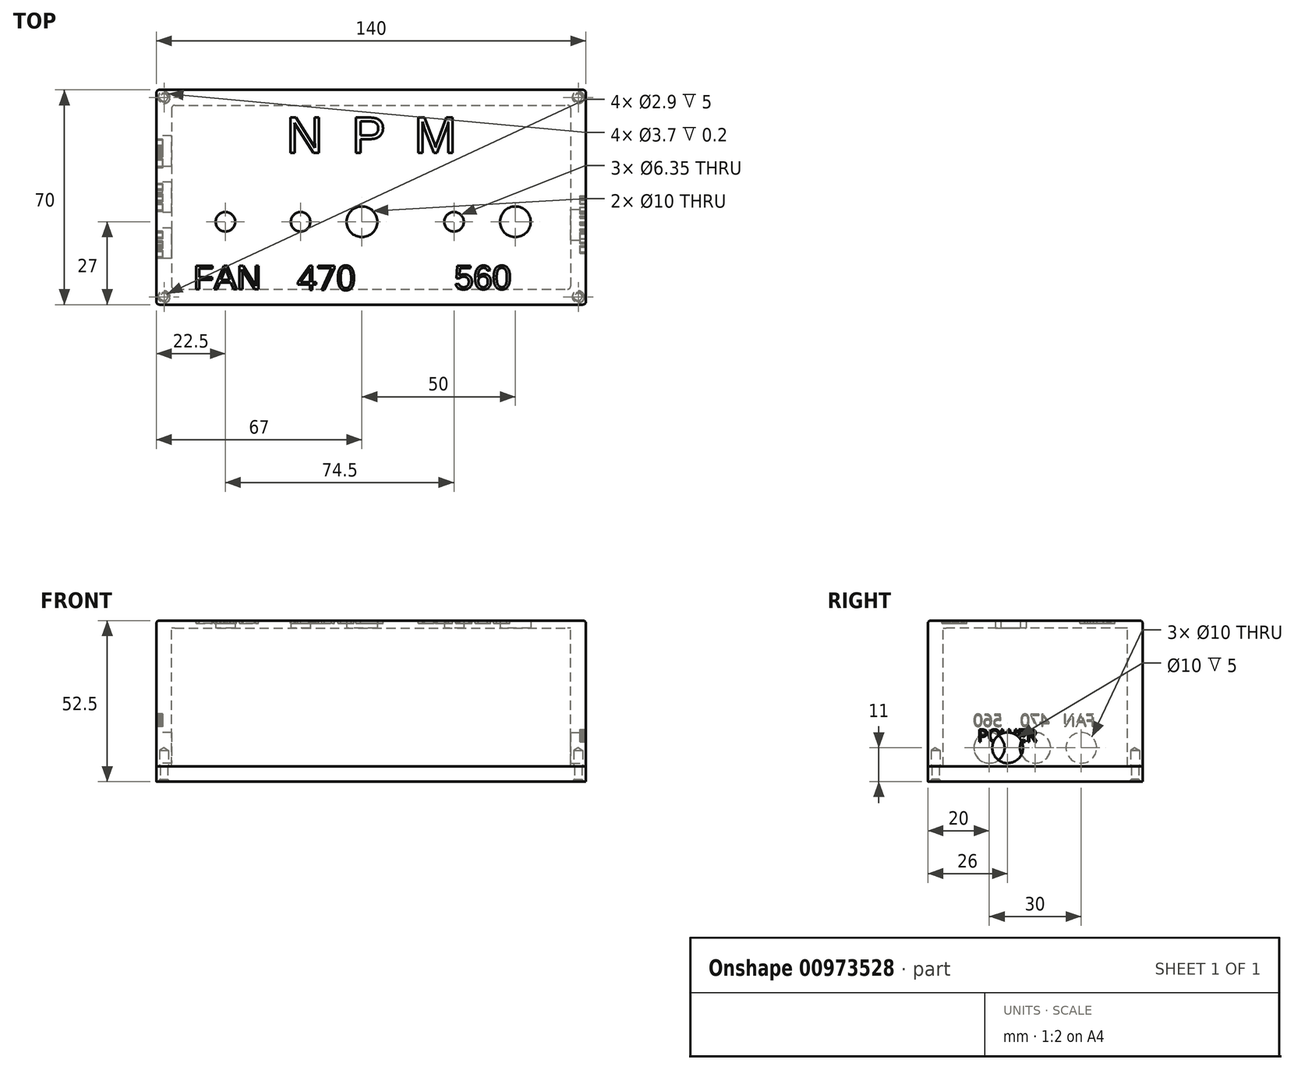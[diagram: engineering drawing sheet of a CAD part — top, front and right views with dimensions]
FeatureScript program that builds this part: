
annotation { "Feature Type Name" : "Feature", "Feature Type Description" : "" }
export const myFeature = defineFeature(function(context is Context, id is Id, definition is map)
    precondition{}
    {
        {
            var Q0;
            Q0=qCreatedBy(makeId("Top.planeOp"),FACE);
            var sketch = newSketch(context, id + "F0", { "sketchPlane" : qUnion([Q0])});
            skLineSegment(sketch, "E0.bottom", {"start": v(0, 0) * mm, "end": v(140, 0) * mm});
            skLineSegment(sketch, "E0.top", {"start": v(0, 70) * mm, "end": v(140, 70) * mm});
            skLineSegment(sketch, "E0.left", {"start": v(0, 0) * mm, "end": v(0, 70) * mm});
            skLineSegment(sketch, "E0.right", {"start": v(140, 0) * mm, "end": v(140, 70) * mm});
            skCircle(sketch, "E1", {"center": v(117, 27) * mm, "radius": 5 * mm});
            skCircle(sketch, "E2", {"center": v(67, 27) * mm, "radius": 5 * mm});
            skCircle(sketch, "E3", {"center": v(22.5, 27) * mm, "radius": 3.18 * mm});
            skLineSegment(sketch, "E4", {"start": v(5, 70) * mm, "end": v(5, 5) * mm, "construction": true});
            skLineSegment(sketch, "E5", {"start": v(5, 5) * mm, "end": v(135, 5) * mm, "construction": true});
            skLineSegment(sketch, "E6", {"start": v(135, 5) * mm, "end": v(135, 70) * mm, "construction": true});
            skLineSegment(sketch, "E7", {"start": v(0, 65) * mm, "end": v(140, 65) * mm, "construction": true});
            skLineSegment(sketch, "E8", {"start": v(5, 5) * mm, "end": v(0, 5) * mm, "construction": true});
            skLineSegment(sketch, "E9", {"start": v(135, 5) * mm, "end": v(140, 5) * mm, "construction": true});
            skPoint(sketch, "E10.endSnap0", {"position": v(5, 37.5) * mm});
            skLineSegment(sketch, "E11", {"start": v(5, 70) * mm, "end": v(135, 65) * mm, "construction": true});
            skLineSegment(sketch, "E12", {"start": v(135, 70) * mm, "end": v(5, 65) * mm, "construction": true});
            skLineSegment(sketch, "E13", {"start": v(140, 5) * mm, "end": v(0, 0) * mm, "construction": true});
            skLineSegment(sketch, "E14", {"start": v(0, 5) * mm, "end": v(140, 0) * mm, "construction": true});
            skPoint(sketch, "E15", {"position": v(70, 2.5) * mm});
            skPoint(sketch, "E16", {"position": v(70, 67.5) * mm});
            skLineSegment(sketch, "E17", {"start": v(5, 27) * mm, "end": v(135, 27) * mm, "construction": true});
            skCircle(sketch, "E18", {"center": v(47, 27) * mm, "radius": 3.18 * mm});
            skCircle(sketch, "E19", {"center": v(97, 27) * mm, "radius": 3.18 * mm});
            skSolve(sketch);
        }
        {
            var Q0;
            Q0=makeQuery(id+"F0.imprint","IMPRINT",FACE,{"disambiguationData":[TD([[makeQuery(id+"F0.imprint","IMPRINT",EDGE,{"derivedFrom":sQuery(id+"F0.wireOp",EDGE,"E0.bottom")}),1.0]])]});
            extrude(context, id + "F1", {"entities" : qUnion([Q0]), "depth" : 2.5 * mm, "offsetDistance" : 25 * mm});
        }
        {
            var Q0;
            Q0=makeQuery(id+"F1.opExtrude","CAP_FACE",FACE,{"disambiguationData":[OSD([sQuery(id+"F0.wireOp",EDGE,"E0.bottom"),sQuery(id+"F0.wireOp",EDGE,"E0.top"),sQuery(id+"F0.wireOp",EDGE,"E0.left"),sQuery(id+"F0.wireOp",EDGE,"E0.right"),sQuery(id+"F0.wireOp",EDGE,"E1"),sQuery(id+"F0.wireOp",EDGE,"E2"),sQuery(id+"F0.wireOp",EDGE,"E3")])],"isStart":true});
            var sketch = newSketch(context, id + "F2", { "sketchPlane" : qUnion([Q0])});
            skLineSegment(sketch, "E20.bottom", {"start": v(0, -70) * mm, "end": v(140, -70) * mm, "construction": true});
            skLineSegment(sketch, "E20.top", {"start": v(0, 0) * mm, "end": v(140, 0) * mm, "construction": true});
            skLineSegment(sketch, "E20.left", {"start": v(0, -70) * mm, "end": v(0, 0) * mm, "construction": true});
            skLineSegment(sketch, "E20.right", {"start": v(140, -70) * mm, "end": v(140, 0) * mm, "construction": true});
            skLineSegment(sketch, "E21.bottom", {"start": v(5, -65) * mm, "end": v(135, -65) * mm});
            skLineSegment(sketch, "E21.top", {"start": v(5, -5) * mm, "end": v(135, -5) * mm});
            skLineSegment(sketch, "E21.left", {"start": v(5, -65) * mm, "end": v(5, -5) * mm});
            skLineSegment(sketch, "E21.right", {"start": v(135, -65) * mm, "end": v(135, -5) * mm});
            skSolve(sketch);
        }
        {
            var Q0;
            Q0=makeQuery(id+"F2.imprint","IMPRINT",FACE,{"disambiguationData":[TD([[makeQuery(id+"F2.imprint","IMPRINT",EDGE,{"derivedFrom":sQuery(id+"F2.wireOp",EDGE,"E21.bottom")}),-1.0]])]});
            var Q1;
            Q1=makeQuery(id+"F2.imprint","IMPRINT",FACE,{"disambiguationData":[TD([[makeQuery(id+"F2.imprint","IMPRINT",EDGE,{"derivedFrom":makeQuery(id+"FxvTJw6m9mzOm3c_1.hole-0.boolean.opBoolean","INTERSECT",EDGE,{"derivedFrom":[makeQuery(id+"F1.opExtrude","CAP_FACE",FACE,{"disambiguationData":[OSD([sQuery(id+"F0.wireOp",EDGE,"E0.bottom"),sQuery(id+"F0.wireOp",EDGE,"E0.top"),sQuery(id+"F0.wireOp",EDGE,"E0.left"),sQuery(id+"F0.wireOp",EDGE,"E0.right"),sQuery(id+"F0.wireOp",EDGE,"E1"),sQuery(id+"F0.wireOp",EDGE,"E2"),sQuery(id+"F0.wireOp",EDGE,"E3")])],"isStart":true}),makeQuery(id+"FxvTJw6m9mzOm3c_1.hole-0.opRevolve","SWEPT_FACE",FACE,{"disambiguationData":[OSD([sQuery(id+"FxvTJw6m9mzOm3c_1.hole-0.sketch.wireOp",EDGE,"core_line_2")])]})]})}),1.0]])]});
            var Q2;
            Q2=makeQuery(id+"F2.imprint","IMPRINT",FACE,{"disambiguationData":[TD([[makeQuery(id+"F2.imprint","IMPRINT",EDGE,{"derivedFrom":makeQuery(id+"FxvTJw6m9mzOm3c_1.hole-1.boolean.opBoolean","INTERSECT",EDGE,{"derivedFrom":[makeQuery(id+"F1.opExtrude","CAP_FACE",FACE,{"disambiguationData":[OSD([sQuery(id+"F0.wireOp",EDGE,"E0.bottom"),sQuery(id+"F0.wireOp",EDGE,"E0.top"),sQuery(id+"F0.wireOp",EDGE,"E0.left"),sQuery(id+"F0.wireOp",EDGE,"E0.right"),sQuery(id+"F0.wireOp",EDGE,"E1"),sQuery(id+"F0.wireOp",EDGE,"E2"),sQuery(id+"F0.wireOp",EDGE,"E3")])],"isStart":true}),makeQuery(id+"FxvTJw6m9mzOm3c_1.hole-1.opRevolve","SWEPT_FACE",FACE,{"disambiguationData":[OSD([sQuery(id+"FxvTJw6m9mzOm3c_1.hole-1.sketch.wireOp",EDGE,"core_line_2")])]})]})}),1.0]])]});
            var Q3;
            Q3=makeQuery(id+"F2.imprint","IMPRINT",FACE,{"disambiguationData":[TD([[makeQuery(id+"F2.imprint","IMPRINT",EDGE,{"derivedFrom":makeQuery(id+"FxvTJw6m9mzOm3c_1.hole-2.boolean.opBoolean","INTERSECT",EDGE,{"derivedFrom":[makeQuery(id+"F1.opExtrude","CAP_FACE",FACE,{"disambiguationData":[OSD([sQuery(id+"F0.wireOp",EDGE,"E0.bottom"),sQuery(id+"F0.wireOp",EDGE,"E0.top"),sQuery(id+"F0.wireOp",EDGE,"E0.left"),sQuery(id+"F0.wireOp",EDGE,"E0.right"),sQuery(id+"F0.wireOp",EDGE,"E1"),sQuery(id+"F0.wireOp",EDGE,"E2"),sQuery(id+"F0.wireOp",EDGE,"E3")])],"isStart":true}),makeQuery(id+"FxvTJw6m9mzOm3c_1.hole-2.opRevolve","SWEPT_FACE",FACE,{"disambiguationData":[OSD([sQuery(id+"FxvTJw6m9mzOm3c_1.hole-2.sketch.wireOp",EDGE,"core_line_2")])]})]})}),1.0]])]});
            var Q4;
            Q4=makeQuery(id+"F2.imprint","IMPRINT",FACE,{"disambiguationData":[TD([[makeQuery(id+"F2.imprint","IMPRINT",EDGE,{"derivedFrom":makeQuery(id+"FxvTJw6m9mzOm3c_1.hole-3.boolean.opBoolean","INTERSECT",EDGE,{"derivedFrom":[makeQuery(id+"F1.opExtrude","CAP_FACE",FACE,{"disambiguationData":[OSD([sQuery(id+"F0.wireOp",EDGE,"E0.bottom"),sQuery(id+"F0.wireOp",EDGE,"E0.top"),sQuery(id+"F0.wireOp",EDGE,"E0.left"),sQuery(id+"F0.wireOp",EDGE,"E0.right"),sQuery(id+"F0.wireOp",EDGE,"E1"),sQuery(id+"F0.wireOp",EDGE,"E2"),sQuery(id+"F0.wireOp",EDGE,"E3")])],"isStart":true}),makeQuery(id+"FxvTJw6m9mzOm3c_1.hole-3.opRevolve","SWEPT_FACE",FACE,{"disambiguationData":[OSD([sQuery(id+"FxvTJw6m9mzOm3c_1.hole-3.sketch.wireOp",EDGE,"core_line_2")])]})]})}),1.0]])]});
            extrude(context, id + "F3", {"entities" : qUnion([Q0, Q1, Q2, Q3, Q4]), "depth" : 45 * mm, "offsetDistance" : 25 * mm});
        }
        {
            var Q0;
            Q0=makeQuery(id+"F3.opExtrude","CAP_FACE",FACE,{"disambiguationData":[OSD([sQuery(id+"F0.wireOp",EDGE,"E0.bottom"),sQuery(id+"F0.wireOp",EDGE,"E0.top"),sQuery(id+"F0.wireOp",EDGE,"E0.left"),sQuery(id+"F0.wireOp",EDGE,"E0.right"),sQuery(id+"F2.wireOp",EDGE,"E21.bottom"),sQuery(id+"F2.wireOp",EDGE,"E21.top"),sQuery(id+"F2.wireOp",EDGE,"E21.left"),sQuery(id+"F2.wireOp",EDGE,"E21.right")])],"isStart":false});
            var sketch = newSketch(context, id + "F4", { "sketchPlane" : qUnion([Q0])});
            skLineSegment(sketch, "E22.bottom", {"start": v(0, 0) * mm, "end": v(140, 0) * mm});
            skLineSegment(sketch, "E22.top", {"start": v(0, -70) * mm, "end": v(140, -70) * mm});
            skLineSegment(sketch, "E22.left", {"start": v(0, 0) * mm, "end": v(0, -70) * mm});
            skLineSegment(sketch, "E22.right", {"start": v(140, 0) * mm, "end": v(140, -70) * mm});
            skLineSegment(sketch, "E23.bottom", {"start": v(5, -5) * mm, "end": v(135, -5) * mm, "construction": true});
            skLineSegment(sketch, "E23.top", {"start": v(5, -65) * mm, "end": v(135, -65) * mm, "construction": true});
            skLineSegment(sketch, "E23.left", {"start": v(5, -5) * mm, "end": v(5, -65) * mm, "construction": true});
            skLineSegment(sketch, "E23.right", {"start": v(135, -5) * mm, "end": v(135, -65) * mm, "construction": true});
            skSolve(sketch);
        }
        {
            var Q0;
            Q0=makeQuery(id+"F4.imprint","IMPRINT",FACE,{"disambiguationData":[TD([[makeQuery(id+"F4.imprint","IMPRINT",EDGE,{"derivedFrom":sQuery(id+"F4.wireOp",EDGE,"E22.bottom")}),-1.0]])]});
            var Q1;
            Q1=makeQuery(id+"F4.imprint","IMPRINT",FACE,{"disambiguationData":[TD([[makeQuery(id+"F4.imprint","IMPRINT",EDGE,{"derivedFrom":makeQuery(id+"F3.opExtrude","CAP_EDGE",EDGE,{"disambiguationData":[OSD([sQuery(id+"F2.wireOp",EDGE,"E21.bottom")])],"isStart":false})}),1.0]])]});
            extrude(context, id + "F5", {"entities" : qUnion([Q0, Q1]), "depth" : 5 * mm, "offsetDistance" : 25 * mm});
        }
        {
            var Q0;
            Q0=makeQuery(id+"F5.opExtrude","CAP_FACE",FACE,{"disambiguationData":[OSD([sQuery(id+"F4.wireOp",EDGE,"E22.bottom"),sQuery(id+"F4.wireOp",EDGE,"E22.top"),sQuery(id+"F4.wireOp",EDGE,"E22.left"),sQuery(id+"F4.wireOp",EDGE,"E22.right")])],"isStart":false});
            var sketch = newSketch(context, id + "F6", { "sketchPlane" : qUnion([Q0])});
            skLineSegment(sketch, "E24.bottom", {"start": v(0, -70) * mm, "end": v(140, -70) * mm, "construction": true});
            skLineSegment(sketch, "E24.top", {"start": v(0, 0) * mm, "end": v(140, 0) * mm, "construction": true});
            skLineSegment(sketch, "E24.left", {"start": v(0, -70) * mm, "end": v(0, 0) * mm, "construction": true});
            skLineSegment(sketch, "E24.right", {"start": v(140, -70) * mm, "end": v(140, 0) * mm, "construction": true});
            skLineSegment(sketch, "E25.bottom", {"start": v(5, -65) * mm, "end": v(135, -65) * mm, "construction": true});
            skLineSegment(sketch, "E25.top", {"start": v(5, -5) * mm, "end": v(135, -5) * mm, "construction": true});
            skLineSegment(sketch, "E25.left", {"start": v(5, -65) * mm, "end": v(5, -5) * mm, "construction": true});
            skLineSegment(sketch, "E25.right", {"start": v(135, -65) * mm, "end": v(135, -5) * mm, "construction": true});
            skLineSegment(sketch, "E26", {"start": v(5, -5) * mm, "end": v(0, 0) * mm, "construction": true});
            skLineSegment(sketch, "E27", {"start": v(135, -5) * mm, "end": v(140, 0) * mm, "construction": true});
            skLineSegment(sketch, "E28", {"start": v(135, -65) * mm, "end": v(140, -70) * mm, "construction": true});
            skLineSegment(sketch, "E29", {"start": v(5, -65) * mm, "end": v(0, -70) * mm, "construction": true});
            skPoint(sketch, "E30", {"position": v(2.5, -2.5) * mm});
            skPoint(sketch, "E31", {"position": v(137.5, -2.5) * mm});
            skPoint(sketch, "E32", {"position": v(137.5, -67.5) * mm});
            skPoint(sketch, "E33", {"position": v(2.5, -67.5) * mm});
            skSolve(sketch);
        }
        {
            var Q0;
            Q0=sQuery(id+"F6.wireOp",VERTEX,"E30");
            var Q1;
            Q1=sQuery(id+"F6.wireOp",VERTEX,"E33");
            var Q2;
            Q2=sQuery(id+"F6.wireOp",VERTEX,"E32");
            var Q3;
            Q3=sQuery(id+"F6.wireOp",VERTEX,"E31");
            var Q4;
            Q4=makeQuery(id+"F3.opExtrude","SWEPT_BODY",BODY,{"disambiguationData":[OSD([sQuery(id+"F0.wireOp",EDGE,"E0.bottom"),sQuery(id+"F0.wireOp",EDGE,"E0.top"),sQuery(id+"F0.wireOp",EDGE,"E0.left"),sQuery(id+"F0.wireOp",EDGE,"E0.right"),sQuery(id+"F2.wireOp",EDGE,"E21.bottom"),sQuery(id+"F2.wireOp",EDGE,"E21.top"),sQuery(id+"F2.wireOp",EDGE,"E21.left"),sQuery(id+"F2.wireOp",EDGE,"E21.right")])]});
            var Q5;
            Q5=makeQuery(id+"F5.opExtrude","SWEPT_BODY",BODY,{"disambiguationData":[OSD([sQuery(id+"F4.wireOp",EDGE,"E22.bottom"),sQuery(id+"F4.wireOp",EDGE,"E22.top"),sQuery(id+"F4.wireOp",EDGE,"E22.left"),sQuery(id+"F4.wireOp",EDGE,"E22.right")])]});
            hole(context, id + "F7", {"style" : HoleStyle.C_SINK, "endStyle" : HoleEndStyle.BLIND, "holeDiameter" : 2.4 * mm, "cSinkDiameter" : 4 * mm, "cSinkAngle" : 90 * degree, "majorDiameter" : 5 * mm, "holeDepth" : 5 * mm, "isTappedThrough" : true, "tappedDepth" : 12 * mm, "tapClearance" : 3, "locations" : qUnion([Q0, Q1, Q2, Q3]), "scope" : qUnion([Q4, Q5])});
        }
        {
            var Q0;
            Q0=makeQuery(id+"F3.opExtrude","CAP_FACE",FACE,{"disambiguationData":[OSD([sQuery(id+"F0.wireOp",EDGE,"E0.bottom"),sQuery(id+"F0.wireOp",EDGE,"E0.top"),sQuery(id+"F0.wireOp",EDGE,"E0.left"),sQuery(id+"F0.wireOp",EDGE,"E0.right"),sQuery(id+"F2.wireOp",EDGE,"E21.bottom"),sQuery(id+"F2.wireOp",EDGE,"E21.top"),sQuery(id+"F2.wireOp",EDGE,"E21.left"),sQuery(id+"F2.wireOp",EDGE,"E21.right")])],"isStart":false});
            var sketch = newSketch(context, id + "F8", { "sketchPlane" : qUnion([Q0])});
            skPoint(sketch, "E34", {"position": v(2.5, -2.5) * mm});
            skPoint(sketch, "E35", {"position": v(2.5, -67.5) * mm});
            skPoint(sketch, "E36", {"position": v(137.5, -67.5) * mm});
            skPoint(sketch, "E37", {"position": v(137.5, -2.5) * mm});
            skSolve(sketch);
        }
        {
            var Q0;
            Q0=sQuery(id+"F8.wireOp",VERTEX,"E34");
            var Q1;
            Q1=sQuery(id+"F8.wireOp",VERTEX,"E35");
            var Q2;
            Q2=sQuery(id+"F8.wireOp",VERTEX,"E36");
            var Q3;
            Q3=sQuery(id+"F8.wireOp",VERTEX,"E37");
            var Q4;
            Q4=makeQuery(id+"F3.opExtrude","SWEPT_BODY",BODY,{"disambiguationData":[OSD([sQuery(id+"F0.wireOp",EDGE,"E0.bottom"),sQuery(id+"F0.wireOp",EDGE,"E0.top"),sQuery(id+"F0.wireOp",EDGE,"E0.left"),sQuery(id+"F0.wireOp",EDGE,"E0.right"),sQuery(id+"F2.wireOp",EDGE,"E21.bottom"),sQuery(id+"F2.wireOp",EDGE,"E21.top"),sQuery(id+"F2.wireOp",EDGE,"E21.left"),sQuery(id+"F2.wireOp",EDGE,"E21.right")])]});
            hole(context, id + "F9", {"style" : HoleStyle.C_BORE, "endStyle" : HoleEndStyle.BLIND, "holeDiameter" : 2.9 * mm, "cBoreDiameter" : 3.7 * mm, "cBoreDepth" : .2 * mm, "majorDiameter" : 5 * mm, "holeDepth" : 5.2 * mm, "isTappedThrough" : true, "tappedDepth" : 12 * mm, "tapClearance" : 3, "locations" : qUnion([Q0, Q1, Q2, Q3]), "scope" : qUnion([Q4])});
        }
        {
            var Q0;
            Q0=makeQuery(id+"F1.opExtrude","CAP_EDGE",EDGE,{"disambiguationData":[OSD([sQuery(id+"F0.wireOp",EDGE,"E0.bottom")])],"isStart":false});
            var Q1;
            Q1=makeQuery(id+"F1.opExtrude","CAP_EDGE",EDGE,{"disambiguationData":[OSD([sQuery(id+"F0.wireOp",EDGE,"E0.left")])],"isStart":false});
            var Q2;
            Q2=makeQuery(id+"F1.opExtrude","CAP_EDGE",EDGE,{"disambiguationData":[OSD([sQuery(id+"F0.wireOp",EDGE,"E0.top")])],"isStart":false});
            var Q3;
            Q3=makeQuery(id+"F1.opExtrude","CAP_EDGE",EDGE,{"disambiguationData":[OSD([sQuery(id+"F0.wireOp",EDGE,"E0.right")])],"isStart":false});
            var Q4;
            Q4=makeQuery(id+"F3.opExtrude","SWEPT_EDGE",EDGE,{"disambiguationData":[OSD([sQuery(id+"F0.wireOp",EDGE,"E0.bottom"),sQuery(id+"F0.wireOp",EDGE,"E0.right")])]});
            var Q5;
            Q5=makeQuery(id+"F3.opExtrude","SWEPT_EDGE",EDGE,{"disambiguationData":[OSD([sQuery(id+"F0.wireOp",EDGE,"E0.bottom"),sQuery(id+"F0.wireOp",EDGE,"E0.left")])]});
            var Q6;
            Q6=makeQuery(id+"F1.opExtrude","SWEPT_EDGE",EDGE,{"disambiguationData":[OSD([sQuery(id+"F0.wireOp",EDGE,"E0.bottom"),sQuery(id+"F0.wireOp",EDGE,"E0.left")])]});
            var Q7;
            Q7=makeQuery(id+"F1.opExtrude","SWEPT_EDGE",EDGE,{"disambiguationData":[OSD([sQuery(id+"F0.wireOp",EDGE,"E0.bottom"),sQuery(id+"F0.wireOp",EDGE,"E0.right")])]});
            var Q8;
            Q8=makeQuery(id+"F3.opExtrude","SWEPT_EDGE",EDGE,{"disambiguationData":[OSD([sQuery(id+"F0.wireOp",EDGE,"E0.top"),sQuery(id+"F0.wireOp",EDGE,"E0.right")])]});
            var Q9;
            Q9=makeQuery(id+"F1.opExtrude","SWEPT_EDGE",EDGE,{"disambiguationData":[OSD([sQuery(id+"F0.wireOp",EDGE,"E0.top"),sQuery(id+"F0.wireOp",EDGE,"E0.right")])]});
            var Q10;
            Q10=makeQuery(id+"F3.opExtrude","SWEPT_EDGE",EDGE,{"disambiguationData":[OSD([sQuery(id+"F0.wireOp",EDGE,"E0.top"),sQuery(id+"F0.wireOp",EDGE,"E0.left")])]});
            var Q11;
            Q11=makeQuery(id+"F1.opExtrude","SWEPT_EDGE",EDGE,{"disambiguationData":[OSD([sQuery(id+"F0.wireOp",EDGE,"E0.top"),sQuery(id+"F0.wireOp",EDGE,"E0.left")])]});
            var Q12;
            Q12=makeQuery(id+"F5.opExtrude","SWEPT_EDGE",EDGE,{"disambiguationData":[OSD([sQuery(id+"F4.wireOp",EDGE,"E22.top"),sQuery(id+"F4.wireOp",EDGE,"E22.left")])]});
            var Q13;
            Q13=makeQuery(id+"F5.opExtrude","SWEPT_EDGE",EDGE,{"disambiguationData":[OSD([sQuery(id+"F4.wireOp",EDGE,"E22.bottom"),sQuery(id+"F4.wireOp",EDGE,"E22.left")])]});
            var Q14;
            Q14=makeQuery(id+"F5.opExtrude","SWEPT_EDGE",EDGE,{"disambiguationData":[OSD([sQuery(id+"F4.wireOp",EDGE,"E22.top"),sQuery(id+"F4.wireOp",EDGE,"E22.right")])]});
            var Q15;
            Q15=makeQuery(id+"F5.opExtrude","SWEPT_EDGE",EDGE,{"disambiguationData":[OSD([sQuery(id+"F4.wireOp",EDGE,"E22.bottom"),sQuery(id+"F4.wireOp",EDGE,"E22.right")])]});
            fillet(context, id + "F10", {"entities" : qUnion([Q0, Q1, Q2, Q3, Q4, Q5, Q6, Q7, Q8, Q9, Q10, Q11, Q12, Q13, Q14, Q15]), "radius" : 1 * mm, "tangentPropagation" : true, "allowEdgeOverflow" : false});
        }
        {
            var Q0;
            Q0=makeQuery(id+"F3.opExtrude","SWEPT_FACE",FACE,{"disambiguationData":[OSD([sQuery(id+"F0.wireOp",EDGE,"E0.left")])]});
            var sketch = newSketch(context, id + "F11", { "sketchPlane" : qUnion([Q0])});
            skCircle(sketch, "E38", {"center": v(-20, -39) * mm, "radius": 5 * mm});
            skLineSegment(sketch, "E39", {"start": v(-35, -45) * mm, "end": v(-35, 0) * mm, "construction": true});
            skLineSegment(sketch, "E40", {"start": v(-20, -39) * mm, "end": v(-70.23, -39) * mm, "construction": true});
            skCircle(sketch, "E41", {"center": v(-35, -39) * mm, "radius": 5 * mm});
            skCircle(sketch, "E42", {"center": v(-50, -39) * mm, "radius": 5 * mm});
            skSolve(sketch);
        }
        {
            var Q0;
            Q0=makeQuery(id+"F3.opExtrude","SWEPT_FACE",FACE,{"disambiguationData":[OSD([sQuery(id+"F0.wireOp",EDGE,"E0.right")])]});
            var sketch = newSketch(context, id + "F12", { "sketchPlane" : qUnion([Q0])});
            skLineSegment(sketch, "E43", {"start": v(1, -39) * mm, "end": v(69, -39) * mm, "construction": true});
            skCircle(sketch, "E44", {"center": v(26, -39) * mm, "radius": 5 * mm});
            skCircle(sketch, "E45", {"center": v(40, -39) * mm, "radius": 5 * mm});
            skCircle(sketch, "E46", {"center": v(54, -39) * mm, "radius": 5 * mm});
            skSolve(sketch);
        }
        {
            var Q0;
            Q0=makeQuery(id+"F10.opFillet","SPLIT",FACE,{"disambiguationData":[OD(4.0)],"derivedFrom":makeQuery(id+"F1.opExtrude","CAP_FACE",FACE,{"disambiguationData":[OSD([sQuery(id+"F0.wireOp",EDGE,"E0.bottom"),sQuery(id+"F0.wireOp",EDGE,"E0.top"),sQuery(id+"F0.wireOp",EDGE,"E0.left"),sQuery(id+"F0.wireOp",EDGE,"E0.right"),sQuery(id+"F0.wireOp",EDGE,"E1"),sQuery(id+"F0.wireOp",EDGE,"E2"),sQuery(id+"F0.wireOp",EDGE,"E3")])],"isStart":false})});
            var sketch = newSketch(context, id + "F13", { "sketchPlane" : qUnion([Q0])});
            skLineSegment(sketch, "E47.bottom", {"start": v(1, 61.5) * mm, "end": v(139, 61.5) * mm, "construction": true});
            skLineSegment(sketch, "E47.top", {"start": v(1, 49.5) * mm, "end": v(139, 49.5) * mm, "construction": true});
            skLineSegment(sketch, "E47.left", {"start": v(1, 61.5) * mm, "end": v(1, 49.5) * mm, "construction": true});
            skLineSegment(sketch, "E47.right", {"start": v(139, 61.5) * mm, "end": v(139, 49.5) * mm, "construction": true});
            skLineSegment(sketch, "E48", {"start": v(70, 61.5) * mm, "end": v(70, 49.5) * mm, "construction": true});
            skLineSegment(sketch, "E49.bottom", {"start": v(87.75, 61.5) * mm, "end": v(42.33, 61.5) * mm, "construction": true});
            skLineSegment(sketch, "E49.top", {"start": v(97.67, 49.5) * mm, "end": v(52.25, 49.5) * mm, "construction": true});
            skLineSegment(sketch, "E49.left", {"start": v(87.75, 61.5) * mm, "end": v(97.67, 49.5) * mm, "construction": true});
            skLineSegment(sketch, "E49.right", {"start": v(42.33, 61.5) * mm, "end": v(52.25, 49.5) * mm, "construction": true});
            skPoint(sketch, "E49.middle", {"position": v(70, 55.5) * mm});
            skText(sketch, "E50", { "text": "N  P  M\n", "fontName": "Arimo-Regular.ttf"});
            const initialGuessF13  = {"E50": [0.04233, 0.0495, 1, 0, 0.012]};
            skSetInitialGuess(sketch, initialGuessF13);
            skSolve(sketch);
        }
        {
            var Q0;
            Q0=qSketchRegion(id+"F13",true);
            extrude(context, id + "F14", {"entities" : qUnion([Q0]), "operationType" : NewBodyOperationType.REMOVE, "oppositeDirection" : true, "depth" : 1 * mm, "offsetDistance" : 25 * mm});
        }
        {
            var Q0;
            Q0=makeQuery(id+"F3.opExtrude","SWEPT_BODY",BODY,{"disambiguationData":[OSD([sQuery(id+"F0.wireOp",EDGE,"E0.bottom"),sQuery(id+"F0.wireOp",EDGE,"E0.top"),sQuery(id+"F0.wireOp",EDGE,"E0.left"),sQuery(id+"F0.wireOp",EDGE,"E0.right"),sQuery(id+"F2.wireOp",EDGE,"E21.bottom"),sQuery(id+"F2.wireOp",EDGE,"E21.top"),sQuery(id+"F2.wireOp",EDGE,"E21.left"),sQuery(id+"F2.wireOp",EDGE,"E21.right")])]});
            var Q1;
            Q1=makeQuery(id+"F1.opExtrude","SWEPT_BODY",BODY,{"disambiguationData":[OSD([sQuery(id+"F0.wireOp",EDGE,"E0.bottom"),sQuery(id+"F0.wireOp",EDGE,"E0.top"),sQuery(id+"F0.wireOp",EDGE,"E0.left"),sQuery(id+"F0.wireOp",EDGE,"E0.right"),sQuery(id+"F0.wireOp",EDGE,"E1"),sQuery(id+"F0.wireOp",EDGE,"E2"),sQuery(id+"F0.wireOp",EDGE,"E3")])]});
            booleanBodies(context, id + "F15", {"operationType" : BooleanOperationType.UNION, "tools" : qUnion([Q0, Q1])});
        }
        {
            var Q0;
            {var subQ0=sQuery(id+"F0.wireOp",EDGE,"E0.right");var subQ1=sQuery(id+"F0.wireOp",EDGE,"E0.left");var subQ2=sQuery(id+"F0.wireOp",EDGE,"E0.top");var subQ3=sQuery(id+"F0.wireOp",EDGE,"E0.bottom");var subQ4=sQuery(id+"F0.wireOp",EDGE,"E3");var subQ5=sQuery(id+"F0.wireOp",EDGE,"E2");var subQ6=sQuery(id+"F0.wireOp",EDGE,"E1");Q0=makeQuery(id+"F14.boolean.opBoolean","SPLIT",FACE,{"disambiguationData":[TD([makeQuery(id+"F1.opExtrude","SWEPT_FACE",FACE,{"disambiguationData":[OSD([subQ6])]})])],"derivedFrom":makeQuery(id+"F1.opExtrude","CAP_FACE",FACE,{"disambiguationData":[OSD([subQ3,subQ2,subQ1,subQ0,subQ6,subQ5,subQ4])],"isStart":false})});}
            var sketch = newSketch(context, id + "F16", { "sketchPlane" : qUnion([Q0])});
            skText(sketch, "E51", { "text": "FAN", "fontName": "Arimo-Regular.ttf"});
            skText(sketch, "E52", { "text": "560\n", "fontName": "Arimo-Regular.ttf"});
            skText(sketch, "E53", { "text": "470\n", "fontName": "OpenSans-Regular.ttf"});
            const initialGuessF16  = {"E51": [0.012, 0.005, 1, 0, 0.008], "E52": [0.09713, 0.005, 1, 0, 0.008], "E53": [0.0459, 0.00472, 1, 0, 0.008]};
            skSetInitialGuess(sketch, initialGuessF16);
            skSolve(sketch);
        }
        {
            var Q0;
            Q0=qSketchRegion(id+"F16",true);
            extrude(context, id + "F17", {"entities" : qUnion([Q0]), "operationType" : NewBodyOperationType.REMOVE, "oppositeDirection" : true, "depth" : 1 * mm, "offsetDistance" : 25 * mm});
        }
        {
            var Q0;
            Q0=makeQuery(id+"F5.opExtrude","CAP_FACE",FACE,{"disambiguationData":[OSD([sQuery(id+"F4.wireOp",EDGE,"E22.bottom"),sQuery(id+"F4.wireOp",EDGE,"E22.top"),sQuery(id+"F4.wireOp",EDGE,"E22.left"),sQuery(id+"F4.wireOp",EDGE,"E22.right")])],"isStart":true});
            var sketch = newSketch(context, id + "F18", { "sketchPlane" : qUnion([Q0])});
            skLineSegment(sketch, "E54", {"start": v(70, 70) * mm, "end": v(70, 0) * mm, "construction": true});
            skLineSegment(sketch, "E55", {"start": v(140, 35) * mm, "end": v(0, 35) * mm, "construction": true});
            skPoint(sketch, "E56", {"position": v(50, 35) * mm});
            skPoint(sketch, "E57", {"position": v(90, 35) * mm});
            skSolve(sketch);
        }
        {
            var Q0;
            Q0=qSketchRegion(id+"F11",true);
            extrude(context, id + "F19", {"entities" : qUnion([Q0]), "operationType" : NewBodyOperationType.REMOVE, "oppositeDirection" : true, "depth" : 25 * mm, "offsetDistance" : 25 * mm});
        }
        {
            var Q0;
            Q0=makeQuery(id+"F12.imprint","IMPRINT",FACE,{"disambiguationData":[TD([[makeQuery(id+"F12.imprint","IMPRINT",EDGE,{"derivedFrom":sQuery(id+"F12.wireOp",EDGE,"E44")}),1.0]])]});
            extrude(context, id + "F20", {"entities" : qUnion([Q0]), "operationType" : NewBodyOperationType.REMOVE, "oppositeDirection" : true, "depth" : 25 * mm, "offsetDistance" : 25 * mm});
        }
        {
            var Q0;
            {var subQ0=sQuery(id+"F0.wireOp",EDGE,"E0.left");Q0=makeQuery(id+"F15.opBoolean","MERGE",FACE,{"derivedFrom":[makeQuery(id+"F1.opExtrude","SWEPT_FACE",FACE,{"disambiguationData":[OSD([subQ0])]}),makeQuery(id+"F3.opExtrude","SWEPT_FACE",FACE,{"disambiguationData":[OSD([subQ0])]})]});}
            var sketch = newSketch(context, id + "F21", { "sketchPlane" : qUnion([Q0])});
            skText(sketch, "E58", { "text": "FAN   470    560\n", "fontName": "OpenSans-Regular.ttf"});
            const initialGuessF21  = {"E58": [-0.0545, -0.032, 1, 0, 0.004]};
            skSetInitialGuess(sketch, initialGuessF21);
            skSolve(sketch);
        }
        {
            var Q0;
            Q0=qSketchRegion(id+"F21",true);
            extrude(context, id + "F22", {"entities" : qUnion([Q0]), "operationType" : NewBodyOperationType.REMOVE, "oppositeDirection" : true, "depth" : 2 * mm, "offsetDistance" : 25 * mm});
        }
        {
            var Q0;
            {var subQ0=sQuery(id+"F0.wireOp",EDGE,"E0.right");Q0=makeQuery(id+"F15.opBoolean","MERGE",FACE,{"derivedFrom":[makeQuery(id+"F1.opExtrude","SWEPT_FACE",FACE,{"disambiguationData":[OSD([subQ0])]}),makeQuery(id+"F3.opExtrude","SWEPT_FACE",FACE,{"disambiguationData":[OSD([subQ0])]})]});}
            var sketch = newSketch(context, id + "F23", { "sketchPlane" : qUnion([Q0])});
            skLineSegment(sketch, "E59", {"start": v(26, -39) * mm, "end": v(26, -35.17) * mm, "construction": true});
            skText(sketch, "E60", { "text": "POWER\n", "fontName": "OpenSans-Regular.ttf"});
            const initialGuessF23  = {"E60": [0.0162, -0.037, 1, 0, 0.004]};
            skSetInitialGuess(sketch, initialGuessF23);
            skSolve(sketch);
        }
        {
            var Q0;
            Q0=qSketchRegion(id+"F23",true);
            extrude(context, id + "F24", {"entities" : qUnion([Q0]), "operationType" : NewBodyOperationType.REMOVE, "oppositeDirection" : true, "depth" : 2 * mm, "offsetDistance" : 25 * mm});
        }
        {
            var Q0;
            Q0=makeQuery(id+"F3.opExtrude","SWEPT_EDGE",EDGE,{"disambiguationData":[OSD([sQuery(id+"F2.wireOp",EDGE,"E21.top"),sQuery(id+"F2.wireOp",EDGE,"E21.left")])]});
            var Q1;
            Q1=makeQuery(id+"F3.opExtrude","SWEPT_EDGE",EDGE,{"disambiguationData":[OSD([sQuery(id+"F2.wireOp",EDGE,"E21.top"),sQuery(id+"F2.wireOp",EDGE,"E21.right")])]});
            var Q2;
            Q2=makeQuery(id+"F3.opExtrude","SWEPT_EDGE",EDGE,{"disambiguationData":[OSD([sQuery(id+"F2.wireOp",EDGE,"E21.bottom"),sQuery(id+"F2.wireOp",EDGE,"E21.right")])]});
            var Q3;
            Q3=makeQuery(id+"F3.opExtrude","SWEPT_EDGE",EDGE,{"disambiguationData":[OSD([sQuery(id+"F2.wireOp",EDGE,"E21.bottom"),sQuery(id+"F2.wireOp",EDGE,"E21.left")])]});
            fillet(context, id + "F25", {"entities" : qUnion([Q0, Q1, Q2, Q3]), "radius" : 1 * mm, "tangentPropagation" : true, "allowEdgeOverflow" : false});
        }
    });
